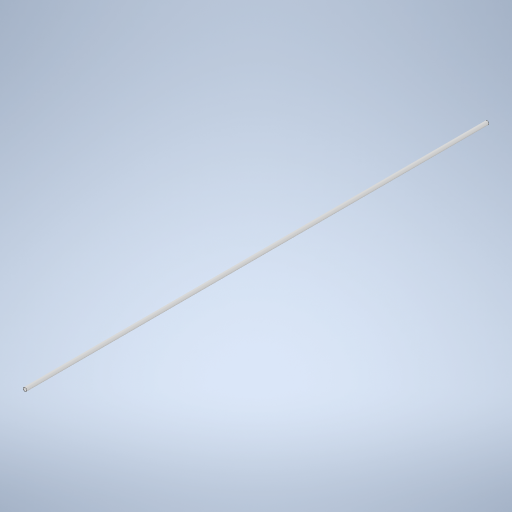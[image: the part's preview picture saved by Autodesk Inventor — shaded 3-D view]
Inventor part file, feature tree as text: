
AUTODESK INVENTOR PART (.ipt)
format: ipt  version: 2023 (Build 270158000, 158)  size: 237,056 bytes
history: native  units: mm
features: extrude x1, sketch x1
ambient origin geometry x8: Origin, YZ Plane, XZ Plane, XY Plane, X Axis, Y Axis, Z Axis, Center Point
bodies: Solido1 (feature_tree)
feature tree (2):
  extrude  "Estrusione1"  Depth=48.26mm
  sketch  "Schizzo1"
